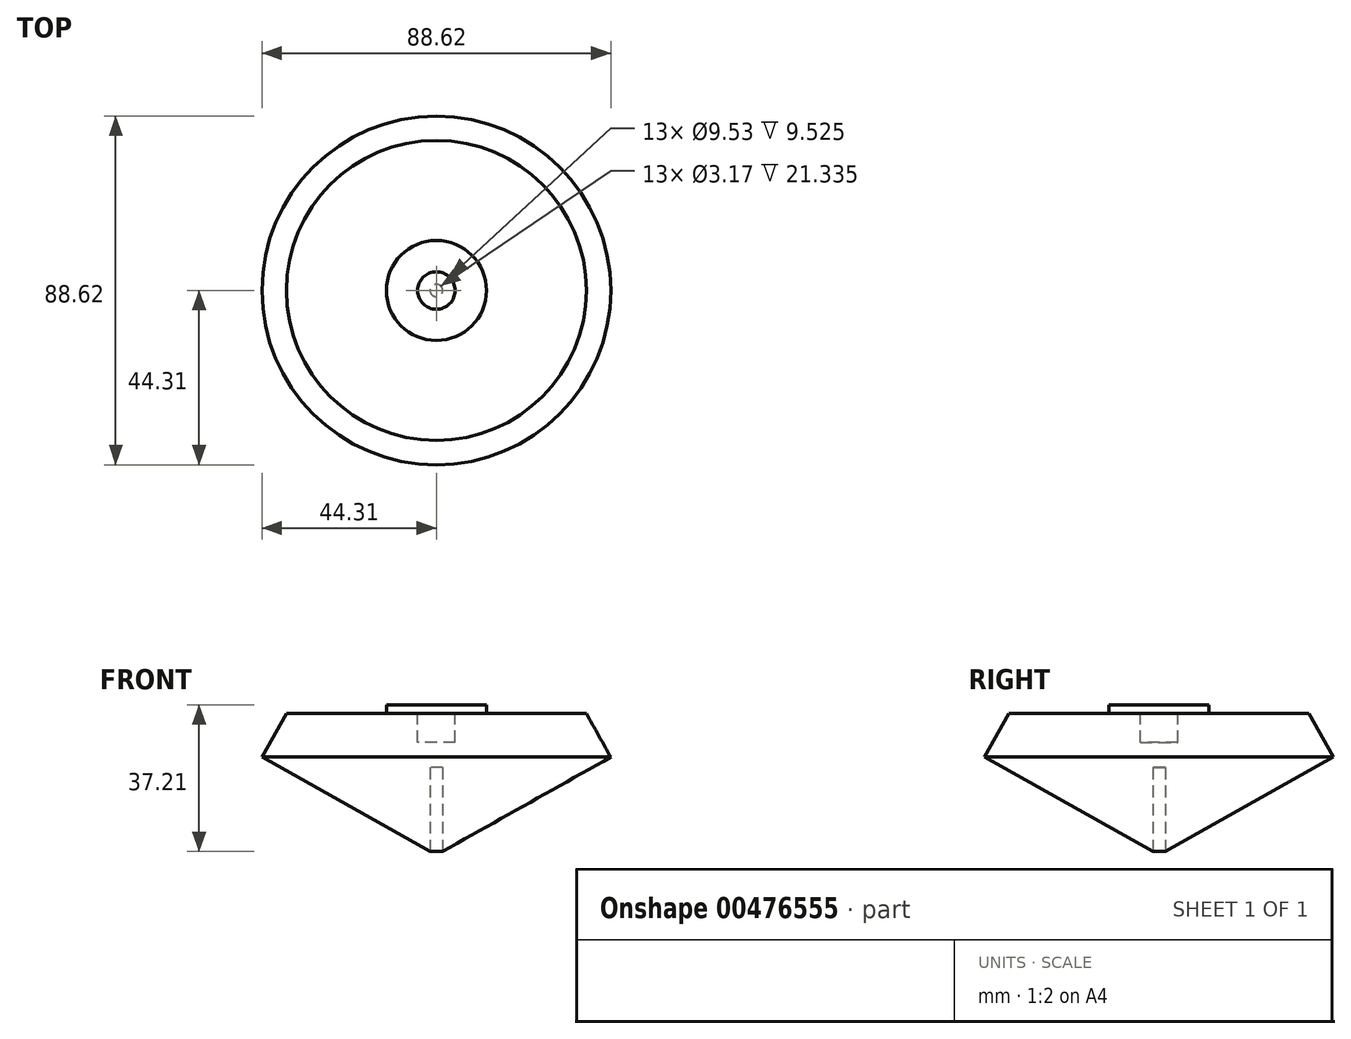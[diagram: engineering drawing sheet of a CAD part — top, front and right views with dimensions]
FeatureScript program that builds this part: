
annotation { "Feature Type Name" : "Feature", "Feature Type Description" : "" }
export const myFeature = defineFeature(function(context is Context, id is Id, definition is map)
    precondition{}
    {
        {
            var Q0;
            Q0=qCreatedBy(makeId("Front.planeOp"),FACE);
            var sketch = newSketch(context, id + "F0", { "sketchPlane" : qUnion([Q0])});
            skLineSegment(sketch, "E0", {"start": v(0, 0) * mm, "end": v(44.31, 24.84) * mm});
            skLineSegment(sketch, "E1", {"start": v(44.31, 24.84) * mm, "end": v(38.1, 35.92) * mm});
            skLineSegment(sketch, "E2", {"start": v(38.1, 35.92) * mm, "end": v(12.7, 35.92) * mm});
            skLineSegment(sketch, "E3", {"start": v(12.7, 35.92) * mm, "end": v(12.7, 38.1) * mm});
            skLineSegment(sketch, "E4", {"start": v(12.7, 38.1) * mm, "end": v(0, 38.1) * mm});
            skLineSegment(sketch, "E5", {"start": v(0, 38.1) * mm, "end": v(0, 0) * mm});
            skSolve(sketch);
        }
        {
            var Q0;
            Q0 = qSketchRegion(id + "F0", true);
            var Q1;
            Q1=sQuery(id+"F0.wireOp",EDGE,"E5");
            revolve(context, id + "F1", {"entities" : qUnion([Q0]), "axis" : qUnion([Q1]), "revolveType" : RevolveType.FULL});
        }
        {
            var Q0;
            Q0=makeQuery(id+"F1.opRevolve","SWEPT_FACE",FACE,{"disambiguationData":[OSD([sQuery(id+"F0.wireOp",EDGE,"E4")])]});
            var sketch = newSketch(context, id + "F2", { "sketchPlane" : qUnion([Q0])});
            skCircle(sketch, "E6", {"center": v(0, 0) * mm, "radius": 4.76 * mm});
            skSolve(sketch);
        }
        {
            var Q0;
            Q0 = qSketchRegion(id + "F2", true);
            extrude(context, id + "F3", {"entities" : qUnion([Q0]), "operationType" : NewBodyOperationType.REMOVE, "oppositeDirection" : true, "depth" : 9.52 * mm});
        }
        {
            var Q0;
            Q0=qCreatedBy(makeId("Top.planeOp"),FACE);
            var sketch = newSketch(context, id + "F4", { "sketchPlane" : qUnion([Q0])});
            skCircle(sketch, "E7", {"center": v(0, 0) * mm, "radius": 1.59 * mm});
            skSolve(sketch);
        }
        {
            var Q0;
            Q0 = qSketchRegion(id + "F4", true);
            extrude(context, id + "F5", {"entities" : qUnion([Q0]), "operationType" : NewBodyOperationType.REMOVE, "depth" : 22.22 * mm});
        }
    });
